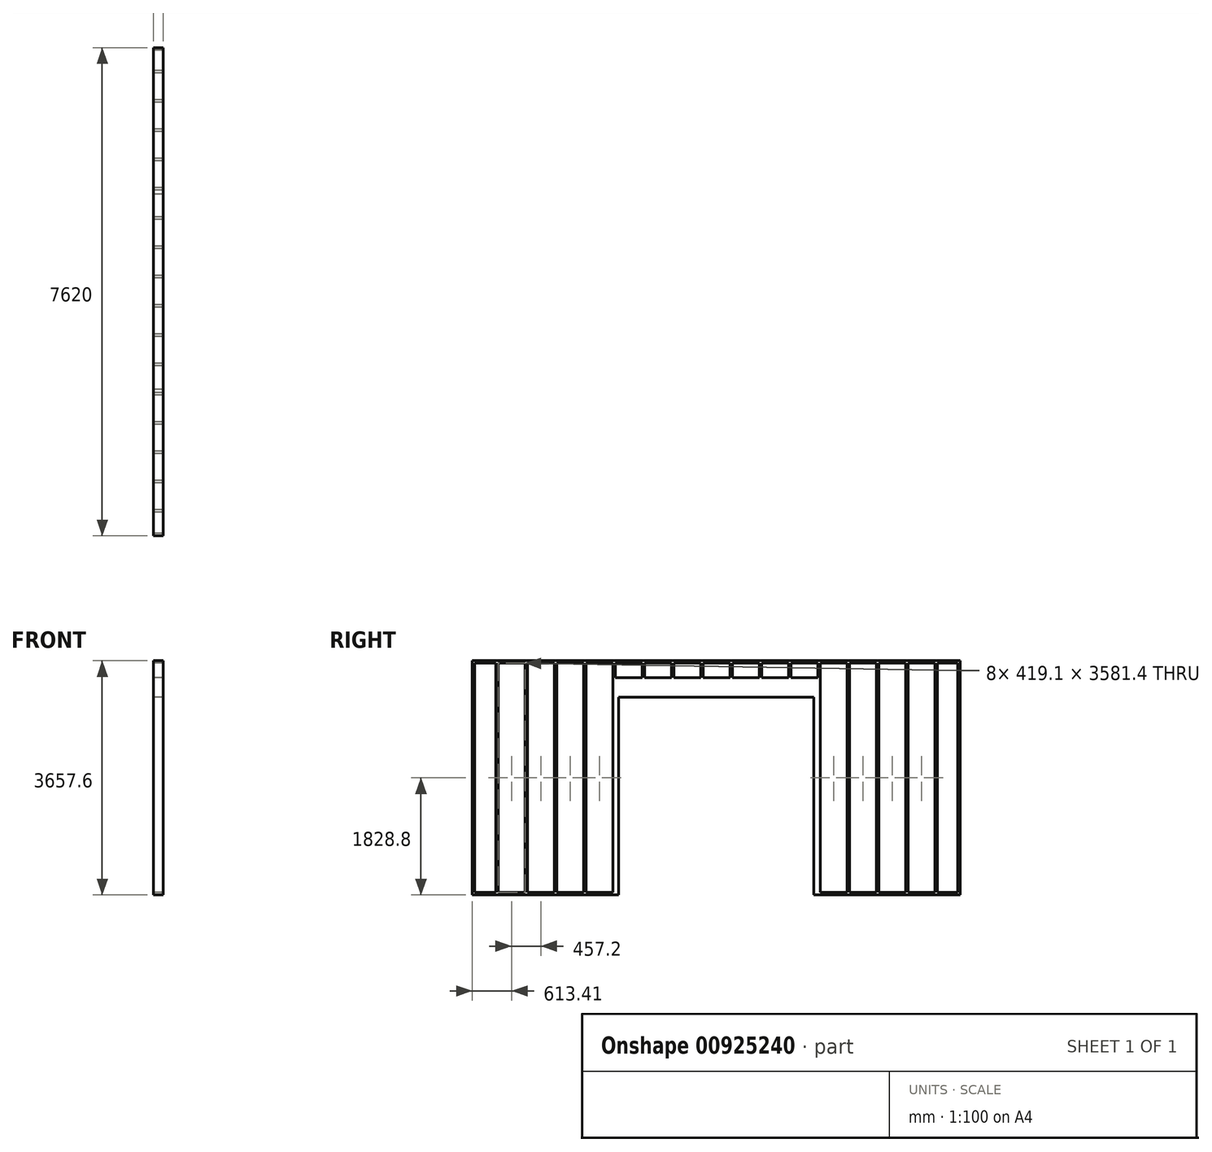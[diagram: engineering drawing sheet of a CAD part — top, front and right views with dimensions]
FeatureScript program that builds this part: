
annotation { "Feature Type Name" : "Feature", "Feature Type Description" : "" }
export const myFeature = defineFeature(function(context is Context, id is Id, definition is map)
    precondition{}
    {
        {
            var Q0;
            Q0=qCreatedBy(makeId("Right.planeOp"),FACE);
            var sketch = newSketch(context, id + "F0", { "sketchPlane" : qUnion([Q0])});
            skLineSegment(sketch, "E0.bottom", {"start": v(0, 0) * mm, "end": v(2286, 0) * mm});
            skLineSegment(sketch, "E0.top", {"start": v(0, 3657.6) * mm, "end": v(7620, 3657.6) * mm});
            skLineSegment(sketch, "E0.left", {"start": v(0, 0) * mm, "end": v(0, 3657.6) * mm});
            skLineSegment(sketch, "E0.right", {"start": v(7620, 0) * mm, "end": v(7620, 3657.6) * mm});
            skLineSegment(sketch, "E1.0", {"start": v(38.1, 38.1) * mm, "end": v(38.1, 3619.5) * mm});
            skLineSegment(sketch, "E1.1", {"start": v(38.1, 38.1) * mm, "end": v(365.76, 38.1) * mm});
            skLineSegment(sketch, "E1.2", {"start": v(7581.9, 38.1) * mm, "end": v(7581.9, 3619.5) * mm});
            skLineSegment(sketch, "E1.3", {"start": v(38.1, 3619.5) * mm, "end": v(365.76, 3619.5) * mm});
            skLineSegment(sketch, "E2", {"start": v(365.76, 3619.5) * mm, "end": v(365.76, 38.1) * mm});
            skLineSegment(sketch, "E3", {"start": v(403.86, 3619.5) * mm, "end": v(403.86, 38.1) * mm});
            skLineSegment(sketch, "E4.trimOffspring", {"start": v(403.86, 3619.5) * mm, "end": v(822.96, 3619.5) * mm});
            skLineSegment(sketch, "E5.trimOffspring", {"start": v(403.86, 38.1) * mm, "end": v(822.96, 38.1) * mm});
            skLineSegment(sketch, "E6.1.0.0", {"start": v(822.96, 3619.5) * mm, "end": v(822.96, 38.1) * mm});
            skLineSegment(sketch, "E6.1.0.1", {"start": v(861.06, 3619.5) * mm, "end": v(861.06, 38.1) * mm});
            skLineSegment(sketch, "E6.2.0.0", {"start": v(1280.16, 3619.5) * mm, "end": v(1280.16, 38.1) * mm});
            skLineSegment(sketch, "E6.2.0.1", {"start": v(1318.26, 3619.5) * mm, "end": v(1318.26, 38.1) * mm});
            skLineSegment(sketch, "E6.3.0.0", {"start": v(1737.36, 3619.5) * mm, "end": v(1737.36, 38.1) * mm});
            skLineSegment(sketch, "E6.3.0.1", {"start": v(1775.46, 3619.5) * mm, "end": v(1775.46, 38.1) * mm});
            skLineSegment(sketch, "E6.4.0.0", {"start": v(2194.56, 3619.5) * mm, "end": v(2194.56, 38.1) * mm});
            skLineSegment(sketch, "E6.4.0.1", {"start": v(2232.66, 3619.5) * mm, "end": v(2232.66, 3390.9) * mm});
            skLineSegment(sketch, "E6.5.0.0", {"start": v(2651.76, 3619.5) * mm, "end": v(2651.76, 3390.9) * mm});
            skLineSegment(sketch, "E6.5.0.1", {"start": v(2689.86, 3619.5) * mm, "end": v(2689.86, 3390.9) * mm});
            skLineSegment(sketch, "E6.6.0.0", {"start": v(3108.96, 3619.5) * mm, "end": v(3108.96, 3390.9) * mm});
            skLineSegment(sketch, "E6.6.0.1", {"start": v(3147.06, 3619.5) * mm, "end": v(3147.06, 3390.9) * mm});
            skLineSegment(sketch, "E6.7.0.0", {"start": v(3566.16, 3619.5) * mm, "end": v(3566.16, 3390.9) * mm});
            skLineSegment(sketch, "E6.7.0.1", {"start": v(3604.26, 3619.5) * mm, "end": v(3604.26, 3390.9) * mm});
            skLineSegment(sketch, "E6.8.0.0", {"start": v(4023.36, 3619.5) * mm, "end": v(4023.36, 3390.9) * mm});
            skLineSegment(sketch, "E6.8.0.1", {"start": v(4061.46, 3619.5) * mm, "end": v(4061.46, 3390.9) * mm});
            skLineSegment(sketch, "E6.9.0.0", {"start": v(4480.56, 3619.5) * mm, "end": v(4480.56, 3390.9) * mm});
            skLineSegment(sketch, "E6.9.0.1", {"start": v(4518.66, 3619.5) * mm, "end": v(4518.66, 3390.9) * mm});
            skLineSegment(sketch, "E6.10.0.0", {"start": v(4937.76, 3619.5) * mm, "end": v(4937.76, 3390.9) * mm});
            skLineSegment(sketch, "E6.10.0.1", {"start": v(4975.86, 3619.5) * mm, "end": v(4975.86, 3390.9) * mm});
            skLineSegment(sketch, "E6.11.0.0", {"start": v(5394.96, 3619.5) * mm, "end": v(5394.96, 3390.9) * mm});
            skLineSegment(sketch, "E6.11.0.1", {"start": v(5433.06, 3619.5) * mm, "end": v(5433.06, 38.1) * mm});
            skLineSegment(sketch, "E6.12.0.0", {"start": v(5852.16, 3619.5) * mm, "end": v(5852.16, 38.1) * mm});
            skLineSegment(sketch, "E6.12.0.1", {"start": v(5890.26, 3619.5) * mm, "end": v(5890.26, 38.1) * mm});
            skLineSegment(sketch, "E6.13.0.0", {"start": v(6309.36, 3619.5) * mm, "end": v(6309.36, 38.1) * mm});
            skLineSegment(sketch, "E6.13.0.1", {"start": v(6347.46, 3619.5) * mm, "end": v(6347.46, 38.1) * mm});
            skLineSegment(sketch, "E6.14.0.0", {"start": v(6766.56, 3619.5) * mm, "end": v(6766.56, 38.1) * mm});
            skLineSegment(sketch, "E6.14.0.1", {"start": v(6804.66, 3619.5) * mm, "end": v(6804.66, 38.1) * mm});
            skLineSegment(sketch, "E6.direction1", {"start": v(403.86, 38.1) * mm, "end": v(822.96, 38.1) * mm, "construction": true});
            skLineSegment(sketch, "E7.trimOffspring", {"start": v(861.06, 3619.5) * mm, "end": v(1280.16, 3619.5) * mm});
            skLineSegment(sketch, "E8.trimOffspring", {"start": v(1318.26, 3619.5) * mm, "end": v(1737.36, 3619.5) * mm});
            skLineSegment(sketch, "E9.trimOffspring", {"start": v(1775.46, 3619.5) * mm, "end": v(2194.56, 3619.5) * mm});
            skLineSegment(sketch, "E10.trimOffspring", {"start": v(2232.66, 3619.5) * mm, "end": v(2651.76, 3619.5) * mm});
            skLineSegment(sketch, "E11.trimOffspring", {"start": v(2689.86, 3619.5) * mm, "end": v(3108.96, 3619.5) * mm});
            skLineSegment(sketch, "E12.trimOffspring", {"start": v(3147.06, 3619.5) * mm, "end": v(3566.16, 3619.5) * mm});
            skLineSegment(sketch, "E13.trimOffspring", {"start": v(3604.26, 3619.5) * mm, "end": v(4023.36, 3619.5) * mm});
            skLineSegment(sketch, "E14.trimOffspring", {"start": v(4061.46, 3619.5) * mm, "end": v(4480.56, 3619.5) * mm});
            skLineSegment(sketch, "E15.trimOffspring", {"start": v(4518.66, 3619.5) * mm, "end": v(4937.76, 3619.5) * mm});
            skLineSegment(sketch, "E16.trimOffspring", {"start": v(4975.86, 3619.5) * mm, "end": v(5394.96, 3619.5) * mm});
            skLineSegment(sketch, "E17.trimOffspring", {"start": v(5433.06, 3619.5) * mm, "end": v(5852.16, 3619.5) * mm});
            skLineSegment(sketch, "E18.trimOffspring", {"start": v(5890.26, 3619.5) * mm, "end": v(6309.36, 3619.5) * mm});
            skLineSegment(sketch, "E19.trimOffspring", {"start": v(6347.46, 3619.5) * mm, "end": v(6766.56, 3619.5) * mm});
            skLineSegment(sketch, "E20.trimOffspring", {"start": v(6804.66, 3619.5) * mm, "end": v(7223.76, 3619.5) * mm});
            skLineSegment(sketch, "E21.trimOffspring", {"start": v(7261.86, 3619.5) * mm, "end": v(7581.9, 3619.5) * mm});
            skLineSegment(sketch, "E22.trimOffspring", {"start": v(7261.86, 38.1) * mm, "end": v(7581.9, 38.1) * mm});
            skLineSegment(sketch, "E23.trimOffspring", {"start": v(6804.66, 38.1) * mm, "end": v(7223.76, 38.1) * mm});
            skLineSegment(sketch, "E24.trimOffspring", {"start": v(6347.46, 38.1) * mm, "end": v(6766.56, 38.1) * mm});
            skLineSegment(sketch, "E25.trimOffspring", {"start": v(5890.26, 38.1) * mm, "end": v(6309.36, 38.1) * mm});
            skLineSegment(sketch, "E26.trimOffspring", {"start": v(5433.06, 38.1) * mm, "end": v(5852.16, 38.1) * mm});
            skLineSegment(sketch, "E27.trimOffspring", {"start": v(1775.46, 38.1) * mm, "end": v(2194.56, 38.1) * mm});
            skLineSegment(sketch, "E28.trimOffspring", {"start": v(1318.26, 38.1) * mm, "end": v(1737.36, 38.1) * mm});
            skLineSegment(sketch, "E29.trimOffspring", {"start": v(861.06, 38.1) * mm, "end": v(1280.16, 38.1) * mm});
            skLineSegment(sketch, "E30.0.15.0", {"start": v(7223.76, 3619.5) * mm, "end": v(7223.76, 38.1) * mm});
            skLineSegment(sketch, "E30.3.15.0", {"start": v(7261.86, 3619.5) * mm, "end": v(7261.86, 38.1) * mm});
            skLineSegment(sketch, "E31.top", {"start": v(2286, 3086.1) * mm, "end": v(5334, 3086.1) * mm});
            skLineSegment(sketch, "E31.left", {"start": v(2286, 38.1) * mm, "end": v(2286, 3086.1) * mm});
            skLineSegment(sketch, "E31.right", {"start": v(5334, 38.1) * mm, "end": v(5334, 3086.1) * mm});
            skLineSegment(sketch, "E32", {"start": v(2232.66, 3390.9) * mm, "end": v(2651.76, 3390.9) * mm});
            skLineSegment(sketch, "E33.trimOffspring", {"start": v(2689.86, 3390.9) * mm, "end": v(3108.96, 3390.9) * mm});
            skLineSegment(sketch, "E34.trimOffspring", {"start": v(3147.06, 3390.9) * mm, "end": v(3566.16, 3390.9) * mm});
            skLineSegment(sketch, "E35.trimOffspring", {"start": v(3604.26, 3390.9) * mm, "end": v(4023.36, 3390.9) * mm});
            skLineSegment(sketch, "E36.trimOffspring", {"start": v(4061.46, 3390.9) * mm, "end": v(4480.56, 3390.9) * mm});
            skLineSegment(sketch, "E37.trimOffspring", {"start": v(4518.66, 3390.9) * mm, "end": v(4937.76, 3390.9) * mm});
            skLineSegment(sketch, "E38.trimOffspring", {"start": v(4975.86, 3390.9) * mm, "end": v(5394.96, 3390.9) * mm});
            skLineSegment(sketch, "E39", {"start": v(2286, 38.1) * mm, "end": v(2286, 0) * mm});
            skLineSegment(sketch, "E40", {"start": v(5334, 38.1) * mm, "end": v(5334, 0) * mm});
            skLineSegment(sketch, "E41.trimOffspring", {"start": v(5334, 0) * mm, "end": v(7620, 0) * mm});
            skSolve(sketch);
        }
        {
            var Q0;
            Q0=qSketchRegion(id+"F0",true);
            extrude(context, id + "F1", {"entities" : qUnion([Q0]), "depth" : 146.3 * mm, "offsetDistance" : 30.48 * mm});
        }
    });
